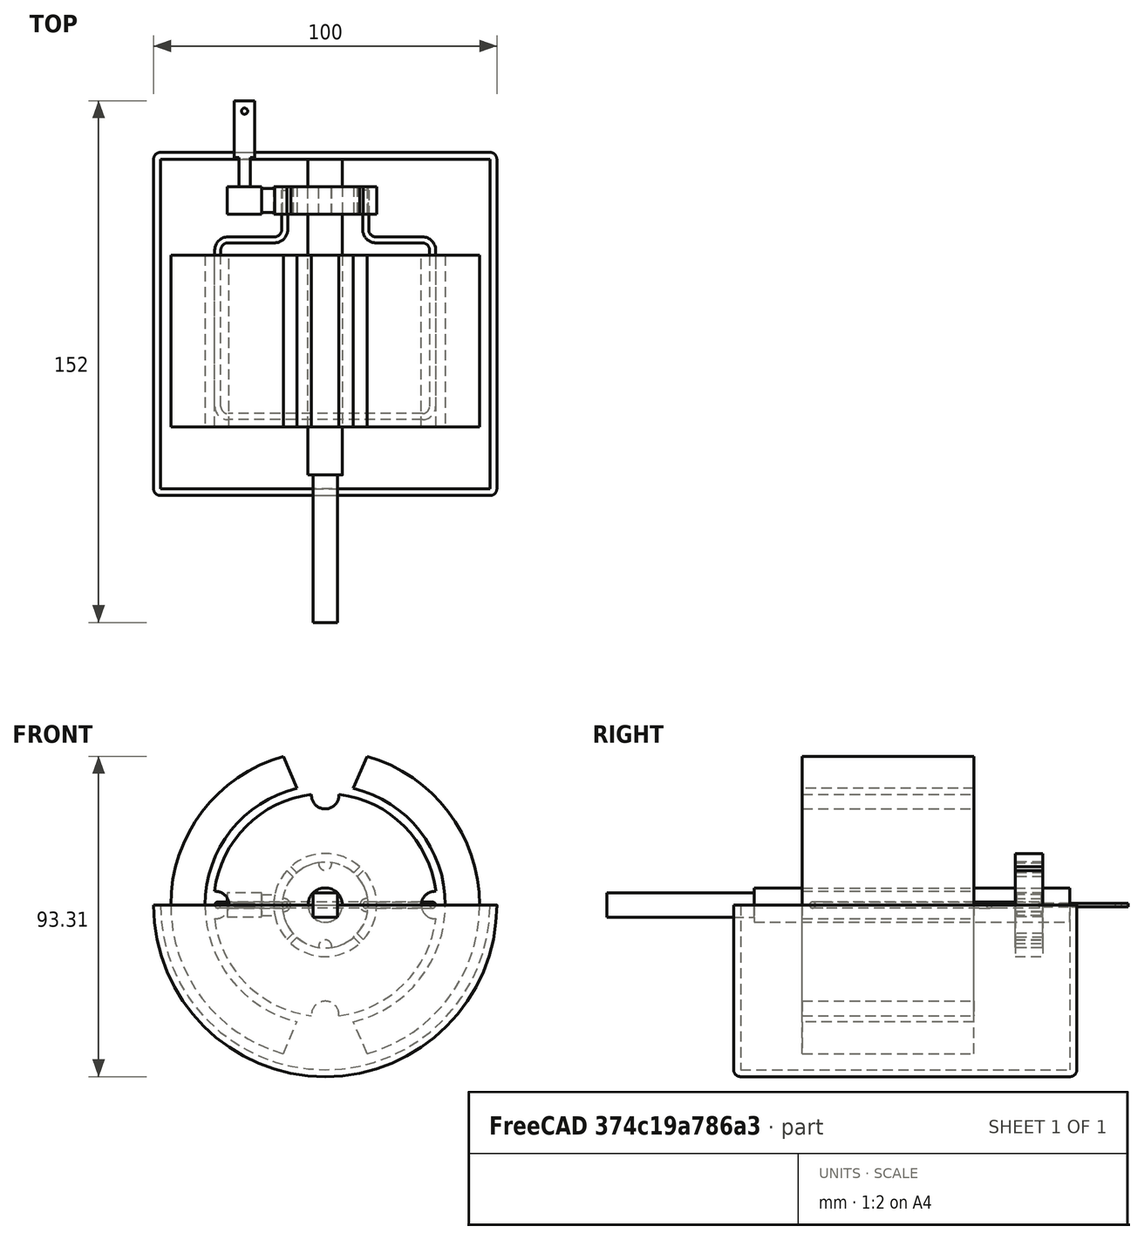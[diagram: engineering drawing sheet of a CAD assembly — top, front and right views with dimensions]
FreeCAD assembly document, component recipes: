
FREECAD ASSEMBLY — COMPONENT RECIPES ("DCmotor")

This assembly document has 15 components, labeled P0..P14 below (a component is one placed body or linked part). 15 of them carry a construction recipe — the FreeCAD feature program that regenerates the part from scratch, quoted from this document or its linked companion documents; the rest are supplied as boundary geometry only. No exploded tour is included for this assembly.
COMPONENT P0 — recipe-attached ("Brush001", modeled in this document).
Construction recipe (the document's own serialized feature program — sketch geometry with constraints, then the solid features built on it; lengths are millimeters unless a unit is written):

FEATURE [Sketcher::SketchObject] Sketch006
  ArcFitTolerance = 1e-06
  AttachmentSupport = -> [XZ_Plane002]
  FullyConstrained = true
  MakeInternals = false
  MapMode = 5
  Placement = pos=(0,0,0) rot=(1,0,0;1.5708rad)
  sketch-geometry (12):
    g0: LineSegment StartX=-18.57 StartY=3 StartZ=0 EndX=-18.57 EndY=-3 EndZ=0
    g1: LineSegment StartX=-18.57 StartY=-3 StartZ=0 EndX=-13.57 EndY=-3 EndZ=0
    g2: LineSegment StartX=-13.57 StartY=-3 StartZ=0 EndX=-13.57 EndY=3 EndZ=0
    g3: LineSegment StartX=-13.57 StartY=3 StartZ=0 EndX=-18.57 EndY=3 EndZ=0
    g4: LineSegment StartX=-28.57 StartY=3.5 StartZ=0 EndX=-28.57 EndY=-3.5 EndZ=0
    g5: LineSegment StartX=-28.57 StartY=-3.5 StartZ=0 EndX=-18.57 EndY=-3.5 EndZ=0
    g6: LineSegment StartX=-18.57 StartY=-3.5 StartZ=0 EndX=-18.57 EndY=3.5 EndZ=0
    g7: LineSegment StartX=-18.57 StartY=3.5 StartZ=0 EndX=-28.57 EndY=3.5 EndZ=0
    g8: LineSegment StartX=-31.07 StartY=0.75 StartZ=0 EndX=-31.07 EndY=-0.75 EndZ=0
    g9: LineSegment StartX=-31.07 StartY=-0.75 StartZ=0 EndX=-28.57 EndY=-0.75 EndZ=0
    g10: LineSegment StartX=-28.57 StartY=-0.75 StartZ=0 EndX=-28.57 EndY=0.75 EndZ=0
    g11: LineSegment StartX=-28.57 StartY=0.75 StartZ=0 EndX=-31.07 EndY=0.75 EndZ=0
  constraints (33):
    c: Coincident(g0,g1)
    c: Coincident(g1,g2)
    c: Coincident(g2,g3)
    c: Coincident(g3,g0)
    c: Vertical(g0)
    c: Horizontal(g1)
    c: Horizontal(g3)
    c: Symmetric(g1,g2,g-1)
    c: DistanceY(g-1,g2) = 3
    c: DistanceX(g0,g2) = 5
    c: DistanceX(g1,g-1) = 13.57
    c: Coincident(g4,g5)
    c: Coincident(g5,g6)
    c: Coincident(g6,g7)
    c: Coincident(g7,g4)
    c: Vertical(g4)
    c: Horizontal(g5)
    c: Horizontal(g7)
    c: Vertical(g6,g0)
    c: DistanceX(g4,g6) = 10
    c: DistanceY(g4,g4) = 7
    c: Symmetric(g5,g6,g-1)
    c: Coincident(g8,g9)
    c: Coincident(g9,g10)
    c: Coincident(g10,g11)
    c: Coincident(g11,g8)
    c: Vertical(g8)
    c: Horizontal(g9)
    c: Horizontal(g11)
    c: Vertical(g9,g4)
    c: Symmetric(g9,g10,g-1)
    c: DistanceY(g8,g8) = 1.5
    c: DistanceX(g8,g9) = 2.5
FEATURE [PartDesign::Pad] Pad002
  Direction = (0,-1,2e-16)
  Length = 8
  Length2 = 10
  Placement = pos=(0,0,0) rot=(1,0,0;1.5708rad)
  Profile = -> Sketch006
  ReferenceAxis = -> Sketch006 [N_Axis]
  Refine = true
  Suppressed = false
  Type = 0
FEATURE [Sketcher::SketchObject] Sketch007
  ArcFitTolerance = 1e-06
  AttachmentSupport = -> [Pad002]
  FullyConstrained = true
  MakeInternals = false
  MapMode = 5
  Placement = pos=(0,-8,4.2e-15) rot=(1,0,0;1.5708rad)
  sketch-geometry (1):
    g0: Circle CenterX=0 CenterY=0 CenterZ=0 NormalX=0 NormalY=0 NormalZ=1 AngleXU=0 Radius=15
  constraints (2):
    c: Diameter(g0) = 30
    c: Coincident(g0,g-1)
FEATURE [PartDesign::Pocket] Pocket004
  BaseFeature = -> Pad002
  Direction = (0,1,-2e-16)
  Length = 5
  Length2 = 5
  Placement = pos=(0,0,0) rot=(1,0,0;1.5708rad)
  Profile = -> Sketch007
  ReferenceAxis = -> Sketch007 [N_Axis]
  Refine = true
  Suppressed = false
  Type = 1
FEATURE [Sketcher::SketchObject] Sketch008
  ArcFitTolerance = 1e-06
  AttachmentSupport = -> [Pocket004]
  ExternalGeometry = -> [Pocket004]
  FullyConstrained = true
  MakeInternals = false
  MapMode = 5
  Placement = pos=(0,3e-16,0.75) rot=(0,0,1;3.14159rad)
  sketch-geometry (8):
    g0: LineSegment StartX=31.07 StartY=8 StartZ=0 EndX=28.57 EndY=8 EndZ=0
    g1: LineSegment StartX=28.57 StartY=8 StartZ=0 EndX=28.57 EndY=3.51 EndZ=0
    g2: LineSegment StartX=28.57 StartY=3.51 StartZ=0 EndX=31.07 EndY=3.51 EndZ=0
    g3: LineSegment StartX=31.07 StartY=3.51 StartZ=0 EndX=31.07 EndY=8 EndZ=0
    g4: LineSegment StartX=28.57 StartY=4.49 StartZ=0 EndX=28.57 EndY=0 EndZ=0
    g5: LineSegment StartX=28.57 StartY=0 StartZ=0 EndX=31.07 EndY=0 EndZ=0
    g6: LineSegment StartX=31.07 StartY=0 StartZ=0 EndX=31.07 EndY=4.49 EndZ=0
    g7: LineSegment StartX=31.07 StartY=4.49 StartZ=0 EndX=28.57 EndY=4.49 EndZ=0
  constraints (23):
    c: Coincident(g0,g1)
    c: Coincident(g1,g2)
    c: Coincident(g2,g3)
    c: Coincident(g3,g0)
    c: Horizontal(g0)
    c: Horizontal(g2)
    c: Vertical(g1)
    c: Vertical(g3)
    c: Coincident(g0,g-4)
    c: PointOnObject(g1,g-3)
    c: Coincident(g4,g5)
    c: Coincident(g5,g6)
    c: Coincident(g6,g7)
    c: Coincident(g7,g4)
    c: Vertical(g4)
    c: Vertical(g6)
    c: Horizontal(g5)
    c: Horizontal(g7)
    c: PointOnObject(g4,g-3)
    c: PointOnObject(g5,g-1)
    c: Vertical(g6,g2)
    c: Equal(g6,g3)
    c: DistanceY(g-1,g2) = 3.51
FEATURE [PartDesign::Pocket] Pocket005
  BaseFeature = -> Pocket004
  Direction = (0,0,-1)
  Length = 5
  Length2 = 5
  Placement = pos=(0,0,0) rot=(1,0,0;1.5708rad)
  Profile = -> Sketch008
  ReferenceAxis = -> Sketch008 [N_Axis]
  Refine = true
  Suppressed = false
  Type = 1
FEATURE [Sketcher::SketchObject] Sketch009
  ArcFitTolerance = 1e-06
  AttachmentSupport = -> [Pocket005]
  ExternalGeometry = -> [Pocket005]
  FullyConstrained = true
  MakeInternals = false
  MapMode = 5
  Placement = pos=(0,1.3e-15,3) rot=(0,0,1;3.14159rad)
  sketch-geometry (8):
    g0: LineSegment StartX=14.6969 StartY=8 StartZ=0 EndX=14.6969 EndY=7.5 EndZ=0
    g1: LineSegment StartX=14.6969 StartY=7.5 StartZ=0 EndX=18.57 EndY=7.5 EndZ=0
    g2: LineSegment StartX=18.57 StartY=7.5 StartZ=0 EndX=18.57 EndY=8 EndZ=0
    g3: LineSegment StartX=18.57 StartY=8 StartZ=0 EndX=14.6969 EndY=8 EndZ=0
    g4: LineSegment StartX=14.6969 StartY=0.5 StartZ=0 EndX=14.6969 EndY=-1e-16 EndZ=0
    g5: LineSegment StartX=14.6969 StartY=-1e-16 StartZ=0 EndX=18.57 EndY=-1e-16 EndZ=0
    g6: LineSegment StartX=18.57 StartY=-1e-16 StartZ=0 EndX=18.57 EndY=0.5 EndZ=0
    g7: LineSegment StartX=18.57 StartY=0.5 StartZ=0 EndX=14.6969 EndY=0.5 EndZ=0
  constraints (22):
    c: Coincident(g0,g1)
    c: Coincident(g1,g2)
    c: Coincident(g2,g3)
    c: Coincident(g3,g0)
    c: Vertical(g0)
    c: Vertical(g2)
    c: Horizontal(g1)
    c: Horizontal(g3)
    c: Coincident(g0,g-5)
    c: PointOnObject(g1,g-4)
    c: DistanceY(g1,g2) = 0.5
    c: Coincident(g4,g5)
    c: Coincident(g5,g6)
    c: Coincident(g6,g7)
    c: Coincident(g7,g4)
    c: Vertical(g4)
    c: Vertical(g6)
    c: Horizontal(g5)
    c: Horizontal(g7)
    c: PointOnObject(g4,g-5)
    c: Coincident(g5,g-4)
    c: DistanceY(g4,g4) = 0.5
FEATURE [PartDesign::Pocket] Pocket006
  BaseFeature = -> Pocket005
  Direction = (0,0,-1)
  Length = 5
  Length2 = 5
  Placement = pos=(0,0,0) rot=(1,0,0;1.5708rad)
  Profile = -> Sketch009
  ReferenceAxis = -> Sketch009 [N_Axis]
  Refine = true
  Suppressed = false
  Type = 1
FEATURE [PartDesign::Body] Body002  label="Brush"
  AllowCompound = false
  Group = -> [Sketch006,Pad002,Sketch007,Pocket004,Sketch008,Pocket005,Sketch009,Pocket006]
  Origin = -> Origin002
  Placement = pos=(0,15,0) rot=(0,0,1;0rad)
  Tip = -> Pocket006
COMPONENT P1 — same part as P0; its construction recipe is shown at P0.
COMPONENT P2 — recipe-attached ("BrushArms001", modeled in this document).
Construction recipe (the document's own serialized feature program — sketch geometry with constraints, then the solid features built on it; lengths are millimeters unless a unit is written):

FEATURE [Sketcher::SketchObject] Sketch016
  ArcFitTolerance = 1e-06
  AttachmentSupport = -> [XY_Plane007]
  FullyConstrained = true
  MakeInternals = false
  MapMode = 5
  sketch-geometry (9):
    g0: LineSegment StartX=-25.16 StartY=15 StartZ=0 EndX=-25.16 EndY=23.5 EndZ=0
    g1: LineSegment StartX=-25.16 StartY=23.5 StartZ=0 EndX=-26.49 EndY=23.5 EndZ=0
    g2: LineSegment StartX=-26.49 StartY=23.5 StartZ=0 EndX=-26.49 EndY=40 EndZ=0
    g3: LineSegment StartX=-26.49 StartY=40 StartZ=0 EndX=-20.5 EndY=40 EndZ=0
    g4: LineSegment StartX=-20.5 StartY=40 StartZ=0 EndX=-20.5 EndY=23.5 EndZ=0
    g5: LineSegment StartX=-20.5 StartY=23.5 StartZ=0 EndX=-21.83 EndY=23.5 EndZ=0
    g6: LineSegment StartX=-21.83 StartY=23.5 StartZ=0 EndX=-21.83 EndY=15 EndZ=0
    g7: LineSegment StartX=-21.83 StartY=15 StartZ=0 EndX=-25.16 EndY=15 EndZ=0
    g8: Circle CenterX=-23.5 CenterY=37 CenterZ=0 NormalX=0 NormalY=0 NormalZ=1 AngleXU=0 Radius=0.9
  constraints (27):
    c: Vertical(g0)
    c: Coincident(g0,g1)
    c: Coincident(g1,g2)
    c: Vertical(g2)
    c: Coincident(g2,g3)
    c: Horizontal(g3)
    c: Coincident(g3,g4)
    c: Vertical(g4)
    c: Coincident(g4,g5)
    c: Horizontal(g5)
    c: Coincident(g5,g6)
    c: Vertical(g6)
    c: Coincident(g6,g7)
    c: Coincident(g7,g0)
    c: Horizontal(g7)
    c: DistanceY(g-1,g0) = 15
    c: Horizontal(g1,g0)
    c: Horizontal(g5,g0)
    c: DistanceX(g6,g-1) = 21.83
    c: DistanceX(g0,g-1) = 25.16
    c: DistanceX(g4,g-1) = 20.5
    c: Equal(g5,g1)
    c: DistanceY(g-1,g4) = 23.5
    c: DistanceY(g-1,g2) = 40
    c: DistanceX(g8,g-1) = 23.5
    c: Diameter(g8) = 1.8
    c: DistanceY(g-1,g8) = 37
FEATURE [PartDesign::Pad] Pad005
  Direction = (0,0,1)
  Length = 1
  Length2 = 10
  Profile = -> Sketch016
  ReferenceAxis = -> Sketch016 [N_Axis]
  Refine = true
  Suppressed = false
  Type = 0
FEATURE [PartDesign::Body] Body006  label="BrushArms"
  AllowCompound = false
  Group = -> [Sketch016,Pad005]
  Origin = -> Origin007
  Placement = pos=(0,0,-0.5) rot=(0,0,1;0rad)
  Tip = -> Pad005
COMPONENT P3 — same part as P2; its construction recipe is shown at P2.
COMPONENT P4 — recipe-attached ("Case001", modeled in this document).
Construction recipe (the document's own serialized feature program — sketch geometry with constraints, then the solid features built on it; lengths are millimeters unless a unit is written):

FEATURE [Sketcher::SketchObject] Sketch021
  ArcFitTolerance = 1e-06
  AttachmentSupport = -> [XZ_Plane010]
  FullyConstrained = true
  MakeInternals = false
  MapMode = 5
  Placement = pos=(0,0,0) rot=(1,0,0;1.5708rad)
  sketch-geometry (2):
    g0: ArcOfCircle CenterX=0 CenterY=0 CenterZ=0 NormalX=0 NormalY=0 NormalZ=1 AngleXU=0 Radius=50 StartAngle=3.14159 EndAngle=6.28319
    g1: LineSegment StartX=50 StartY=-1.22e-14 StartZ=0 EndX=-50 EndY=1.73205e-05 EndZ=0
  constraints (6):
    c: Angle(g0) = 3.14159
    c: Coincident(g0,g-1)
    c: PointOnObject(g0,g-1)
    c: DistanceX(g-1,g0) = 50
    c: Coincident(g1,g0)
    c: Coincident(g1,g0)
FEATURE [PartDesign::Pad] Pad008
  Direction = (0,-1,2e-16)
  Length = 100
  Length2 = 10
  Placement = pos=(0,0,0) rot=(1,0,0;1.5708rad)
  Profile = -> Sketch021
  ReferenceAxis = -> Sketch021 [N_Axis]
  Refine = true
  Suppressed = false
  Type = 0
FEATURE [Sketcher::SketchObject] Sketch022
  ArcFitTolerance = 1e-06
  AttachmentSupport = -> [XZ_Plane010]
  FullyConstrained = true
  MakeInternals = false
  MapMode = 5
  Placement = pos=(0,0,0) rot=(1,0,0;1.5708rad)
  sketch-geometry (2):
    g0: ArcOfCircle CenterX=0 CenterY=0 CenterZ=0 NormalX=0 NormalY=0 NormalZ=1 AngleXU=0 Radius=48 StartAngle=3.14159 EndAngle=6.28319
    g1: LineSegment StartX=48 StartY=0 StartZ=0 EndX=-48 EndY=5.9e-15 EndZ=0
  constraints (6):
    c: Radius(g0) = 48
    c: Coincident(g0,g-1)
    c: PointOnObject(g0,g-1)
    c: PointOnObject(g0,g-1)
    c: Coincident(g1,g0)
    c: Coincident(g1,g0)
FEATURE [PartDesign::Pocket] Pocket011
  BaseFeature = -> Pad008
  Direction = (0,1,-2e-16)
  Length = 5
  Length2 = 5
  Placement = pos=(0,0,0) rot=(1,0,0;1.5708rad)
  Profile = -> Sketch022
  ReferenceAxis = -> Sketch022 [N_Axis]
  Refine = true
  Reversed = true
  Suppressed = false
  Type = 1
FEATURE [Sketcher::SketchObject] Sketch023
  ArcFitTolerance = 1e-06
  AttachmentSupport = -> [XZ_Plane010]
  FullyConstrained = true
  MakeInternals = false
  MapMode = 5
  Placement = pos=(0,0,0) rot=(1,0,0;1.5708rad)
  sketch-geometry (2):
    g0: ArcOfCircle CenterX=0 CenterY=0 CenterZ=0 NormalX=0 NormalY=0 NormalZ=1 AngleXU=0 Radius=48.02 StartAngle=3.14159 EndAngle=6.28319
    g1: LineSegment StartX=-48.02 StartY=0 StartZ=0 EndX=48.02 EndY=0 EndZ=0
  constraints (6):
    c: Radius(g0) = 48.02
    c: Coincident(g0,g-1)
    c: PointOnObject(g0,g-1)
    c: PointOnObject(g0,g-1)
    c: Coincident(g1,g0)
    c: Coincident(g1,g0)
FEATURE [PartDesign::Pad] Pad009
  BaseFeature = -> Pocket011
  Direction = (0,-1,2e-16)
  Length = 2
  Length2 = 10
  Placement = pos=(0,0,0) rot=(1,0,0;1.5708rad)
  Profile = -> Sketch023
  ReferenceAxis = -> Sketch023 [N_Axis]
  Refine = true
  Suppressed = false
  Type = 0
FEATURE [Sketcher::SketchObject] Sketch024
  ArcFitTolerance = 1e-06
  AttachmentSupport = -> [Pad009]
  FullyConstrained = true
  MakeInternals = false
  MapMode = 5
  Placement = pos=(0,-100,2.2e-14) rot=(1,0,0;1.5708rad)
  sketch-geometry (2):
    g0: ArcOfCircle CenterX=0 CenterY=0 CenterZ=0 NormalX=0 NormalY=0 NormalZ=1 AngleXU=0 Radius=48.02 StartAngle=3.14159 EndAngle=6.28319
    g1: LineSegment StartX=-48.02 StartY=5.9e-15 StartZ=0 EndX=48.02 EndY=0 EndZ=0
  constraints (6):
    c: Radius(g0) = 48.02
    c: Coincident(g0,g-1)
    c: PointOnObject(g0,g-1)
    c: PointOnObject(g0,g-1)
    c: Coincident(g1,g0)
    c: Coincident(g1,g0)
FEATURE [PartDesign::Pad] Pad010
  BaseFeature = -> Pad009
  Direction = (0,-1,2e-16)
  Length = 2
  Length2 = 10
  Placement = pos=(0,0,0) rot=(1,0,0;1.5708rad)
  Profile = -> Sketch024
  ReferenceAxis = -> Sketch024 [N_Axis]
  Refine = true
  Reversed = true
  Suppressed = false
  Type = 0
FEATURE [PartDesign::Fillet] Fillet
  Base = -> Pad010 [Edge8]
  BaseFeature = -> Pad010
  Placement = pos=(0,0,0) rot=(1,0,0;1.5708rad)
  Radius = 2
  Refine = true
  SupportTransform = false
  Suppressed = false
  UseAllEdges = false
FEATURE [PartDesign::Fillet] Fillet001
  Base = -> Fillet [Edge3]
  BaseFeature = -> Fillet
  Placement = pos=(0,0,0) rot=(1,0,0;1.5708rad)
  Radius = 2
  Refine = true
  SupportTransform = false
  Suppressed = false
  UseAllEdges = false
FEATURE [Sketcher::SketchObject] Sketch025
  ArcFitTolerance = 1e-06
  AttachmentSupport = -> [XZ_Plane010]
  FullyConstrained = true
  MakeInternals = false
  MapMode = 5
  Placement = pos=(0,0,0) rot=(1,0,0;1.5708rad)
FEATURE [PartDesign::Body] Body009  label="Case"
  AllowCompound = false
  Group = -> [Sketch021,Pad008,Sketch022,Pocket011,Sketch023,Pad009,Sketch024,Pad010,Fillet,Fillet001,Sketch025]
  Origin = -> Origin010
  Placement = pos=(0,25,0) rot=(0,0,1;0rad)
  Tip = -> Fillet001
COMPONENT P5 — same part as P4; its construction recipe is shown at P4.
COMPONENT P6 — recipe-attached ("Commutator001", modeled in this document).
Construction recipe (the document's own serialized feature program — sketch geometry with constraints, then the solid features built on it; lengths are millimeters unless a unit is written):

FEATURE [Sketcher::SketchObject] Sketch
  ArcFitTolerance = 1e-06
  AttachmentSupport = -> [XZ_Plane]
  FullyConstrained = true
  MakeInternals = false
  MapMode = 5
  Placement = pos=(0,0,0) rot=(1,0,0;1.5708rad)
  sketch-geometry (1):
    g0: Circle CenterX=0 CenterY=0 CenterZ=0 NormalX=0 NormalY=0 NormalZ=1 AngleXU=0 Radius=15
  constraints (2):
    c: Coincident(g0,g-1)
    c: Diameter(g0) = 30
FEATURE [PartDesign::Pad] Pad
  Direction = (0,-1,2e-16)
  Length = 8
  Length2 = 10
  Placement = pos=(0,0,0) rot=(1,0,0;1.5708rad)
  Profile = -> Sketch
  ReferenceAxis = -> Sketch [N_Axis]
  Refine = true
  Suppressed = false
  Type = 0
FEATURE [Sketcher::SketchObject] Sketch001
  ArcFitTolerance = 1e-06
  AttachmentSupport = -> [Pad]
  FullyConstrained = true
  MakeInternals = false
  MapMode = 5
  Placement = pos=(0,-8,0) rot=(1,0,0;1.5708rad)
  sketch-geometry (1):
    g0: Circle CenterX=0 CenterY=0 CenterZ=0 NormalX=0 NormalY=0 NormalZ=1 AngleXU=0 Radius=12.5
  constraints (2):
    c: Diameter(g0) = 25
    c: Coincident(g0,g-1)
FEATURE [PartDesign::Pocket] Pocket
  BaseFeature = -> Pad
  Direction = (0,1,-2e-16)
  Length = 5
  Length2 = 5
  Placement = pos=(0,0,0) rot=(1,0,0;1.5708rad)
  Profile = -> Sketch001
  ReferenceAxis = -> Sketch001 [N_Axis]
  Refine = true
  Suppressed = false
  Type = 1
FEATURE [Sketcher::SketchObject] Sketch002
  ArcFitTolerance = 1e-06
  AttachmentSupport = -> [Pocket]
  ExternalGeometry = -> [Pocket]
  FullyConstrained = true
  MakeInternals = false
  MapMode = 5
  Placement = pos=(0,-8,0) rot=(1,0,0;1.5708rad)
  sketch-geometry (8):
    g0: LineSegment StartX=-0.75 StartY=18.87 StartZ=0 EndX=-0.75 EndY=-18.87 EndZ=0
    g1: LineSegment StartX=-0.75 StartY=-18.87 StartZ=0 EndX=0.75 EndY=-18.87 EndZ=0
    g2: LineSegment StartX=0.75 StartY=-18.87 StartZ=0 EndX=0.75 EndY=18.87 EndZ=0
    g3: LineSegment StartX=0.75 StartY=18.87 StartZ=0 EndX=-0.75 EndY=18.87 EndZ=0
    g4: LineSegment StartX=-17.13 StartY=0.75 StartZ=0 EndX=-17.13 EndY=-0.75 EndZ=0
    g5: LineSegment StartX=-17.13 StartY=-0.75 StartZ=0 EndX=17.73 EndY=-0.75 EndZ=0
    g6: LineSegment StartX=17.73 StartY=-0.75 StartZ=0 EndX=17.73 EndY=0.75 EndZ=0
    g7: LineSegment StartX=17.73 StartY=0.75 StartZ=0 EndX=-17.13 EndY=0.75 EndZ=0
  constraints (21):
    c: Coincident(g0,g1)
    c: Coincident(g1,g2)
    c: Coincident(g2,g3)
    c: Coincident(g3,g0)
    c: Vertical(g0)
    c: Horizontal(g1)
    c: Symmetric(g0,g2,g-2)
    c: DistanceX(g0,g-1) = 0.75
    c: Coincident(g4,g5)
    c: Coincident(g5,g6)
    c: Coincident(g6,g7)
    c: Coincident(g7,g4)
    c: Vertical(g4)
    c: Horizontal(g5)
    c: Horizontal(g7)
    c: Symmetric(g5,g6,g-1)
    c: DistanceY(g5,g-1) = 0.75
    c: Symmetric(g1,g2,g-1)
    c: DistanceY(g1,g-1) = 18.87
    c: DistanceX(g4,g-1) = 17.13
    c: DistanceX(g-1,g5) = 17.73
FEATURE [PartDesign::Pocket] Pocket001
  BaseFeature = -> Pocket
  Direction = (0,1,-2e-16)
  Length = 5
  Length2 = 5
  Placement = pos=(0,0,0) rot=(1,0,0;1.5708rad)
  Profile = -> Sketch002
  ReferenceAxis = -> Sketch002 [N_Axis]
  Refine = true
  Suppressed = false
  Type = 1
FEATURE [PartDesign::Body] Body  label="Commutator"
  AllowCompound = true
  Group = -> [Sketch,Pad,Sketch001,Pocket,Sketch002,Pocket001]
  Origin = -> Origin
  Placement = pos=(0,15,1.08e-14) rot=(0,1,0;0.785398rad)
  Tip = -> Pocket001
COMPONENT P7 — recipe-attached ("CommutatorSupport001", modeled in this document).
Construction recipe (the document's own serialized feature program — sketch geometry with constraints, then the solid features built on it; lengths are millimeters unless a unit is written):

FEATURE [Sketcher::SketchObject] Sketch017
  ArcFitTolerance = 1e-06
  AttachmentSupport = -> [XZ_Plane008]
  FullyConstrained = true
  MakeInternals = false
  MapMode = 5
  Placement = pos=(0,0,0) rot=(1,0,0;1.5708rad)
  sketch-geometry (1):
    g0: Circle CenterX=0 CenterY=0 CenterZ=0 NormalX=0 NormalY=0 NormalZ=1 AngleXU=0 Radius=12.5
  constraints (2):
    c: Diameter(g0) = 25
    c: Coincident(g0,g-1)
FEATURE [PartDesign::Pad] Pad006
  Direction = (0,-1,2e-16)
  Length = 8
  Length2 = 10
  Placement = pos=(0,0,0) rot=(1,0,0;1.5708rad)
  Profile = -> Sketch017
  ReferenceAxis = -> Sketch017 [N_Axis]
  Refine = true
  Suppressed = false
  Type = 0
FEATURE [Sketcher::SketchObject] Sketch018
  ArcFitTolerance = 1e-06
  AttachmentSupport = -> [XZ_Plane008]
  FullyConstrained = true
  MakeInternals = false
  MapMode = 5
  Placement = pos=(0,0,0) rot=(1,0,0;1.5708rad)
  sketch-geometry (4):
    g0: Circle CenterX=12 CenterY=0 CenterZ=0 NormalX=0 NormalY=0 NormalZ=1 AngleXU=0 Radius=1.875
    g1: Circle CenterX=-12 CenterY=0 CenterZ=0 NormalX=0 NormalY=0 NormalZ=1 AngleXU=0 Radius=1.875
    g2: Circle CenterX=0 CenterY=12 CenterZ=0 NormalX=0 NormalY=0 NormalZ=1 AngleXU=0 Radius=1.875
    g3: Circle CenterX=0 CenterY=-12 CenterZ=0 NormalX=0 NormalY=0 NormalZ=1 AngleXU=0 Radius=1.875
  constraints (10):
    c: Diameter(g0) = 3.75
    c: PointOnObject(g0,g-1)
    c: DistanceX(g-1,g0) = 12
    c: Symmetric(g1,g0,g-2)
    c: Equal(g1,g0)
    c: PointOnObject(g2,g-2)
    c: Equal(g2,g1)
    c: DistanceY(g-1,g2) = 12
    c: Equal(g3,g1)
    c: Symmetric(g3,g2,g-1)
FEATURE [PartDesign::Pocket] Pocket009
  BaseFeature = -> Pad006
  Direction = (0,1,-2e-16)
  Length = 5
  Length2 = 5
  Placement = pos=(0,0,0) rot=(1,0,0;1.5708rad)
  Profile = -> Sketch018
  ReferenceAxis = -> Sketch018 [N_Axis]
  Refine = true
  Reversed = true
  Suppressed = false
  Type = 1
FEATURE [PartDesign::Body] Body007  label="CommutatorSupport"
  AllowCompound = false
  Group = -> [Sketch017,Pad006,Sketch018,Pocket009]
  Origin = -> Origin008
  Placement = pos=(0,15,0) rot=(0,1,0;0rad)
  Tip = -> Pocket009
COMPONENT P8 — recipe-attached ("NorthMagnet001", modeled in this document).
Construction recipe (the document's own serialized feature program — sketch geometry with constraints, then the solid features built on it; lengths are millimeters unless a unit is written):

FEATURE [Sketcher::SketchObject] Sketch003
  ArcFitTolerance = 1e-06
  AttachmentSupport = -> [XZ_Plane001]
  FullyConstrained = true
  MakeInternals = false
  MapMode = 5
  Placement = pos=(0,0,0) rot=(1,0,0;1.5708rad)
  sketch-geometry (1):
    g0: Circle CenterX=0 CenterY=0 CenterZ=0 NormalX=0 NormalY=0 NormalZ=1 AngleXU=0 Radius=45
  constraints (2):
    c: Coincident(g0,g-1)
    c: Diameter(g0) = 90
FEATURE [PartDesign::Pad] Pad001
  Direction = (0,-1,2e-16)
  Length = 50
  Length2 = 10
  Placement = pos=(0,0,0) rot=(1,0,0;1.5708rad)
  Profile = -> Sketch003
  ReferenceAxis = -> Sketch003 [N_Axis]
  Refine = true
  Suppressed = false
  Type = 0
FEATURE [Sketcher::SketchObject] Sketch004
  ArcFitTolerance = 1e-06
  AttachmentSupport = -> [Pad001]
  FullyConstrained = true
  MakeInternals = false
  MapMode = 5
  Placement = pos=(0,-50,0) rot=(1,0,0;1.5708rad)
  sketch-geometry (1):
    g0: Circle CenterX=0 CenterY=0 CenterZ=0 NormalX=0 NormalY=0 NormalZ=1 AngleXU=0 Radius=35
  constraints (2):
    c: Diameter(g0) = 70
    c: Coincident(g0,g-1)
FEATURE [PartDesign::Pocket] Pocket002
  BaseFeature = -> Pad001
  Direction = (0,1,-2e-16)
  Length = 5
  Length2 = 5
  Placement = pos=(0,0,0) rot=(1,0,0;1.5708rad)
  Profile = -> Sketch004
  ReferenceAxis = -> Sketch004 [N_Axis]
  Refine = true
  Suppressed = false
  Type = 1
FEATURE [Sketcher::SketchObject] Sketch005
  ArcFitTolerance = 1e-06
  AttachmentSupport = -> [Pocket002]
  ExternalGeometry = -> [Pocket002]
  FullyConstrained = true
  MakeInternals = false
  MapMode = 5
  Placement = pos=(0,-50,0) rot=(1,0,0;1.5708rad)
  sketch-geometry (8):
    g0: LineSegment StartX=-13 StartY=45.18 StartZ=0 EndX=13 EndY=45.18 EndZ=0
    g1: LineSegment StartX=-8.2 StartY=34 StartZ=0 EndX=8.2 EndY=34 EndZ=0
    g2: LineSegment StartX=-13 StartY=45.18 StartZ=0 EndX=-8.2 EndY=34 EndZ=0
    g3: LineSegment StartX=8.2 StartY=34 StartZ=0 EndX=13 EndY=45.18 EndZ=0
    g4: LineSegment StartX=-8.2 StartY=-34 StartZ=0 EndX=8.2 EndY=-34 EndZ=0
    g5: LineSegment StartX=8.2 StartY=-34 StartZ=0 EndX=13 EndY=-45.18 EndZ=0
    g6: LineSegment StartX=13 StartY=-45.18 StartZ=0 EndX=-13 EndY=-45.18 EndZ=0
    g7: LineSegment StartX=-13 StartY=-45.18 StartZ=0 EndX=-8.2 EndY=-34 EndZ=0
  constraints (20):
    c: DistanceX(g0,g-1) = 13
    c: Symmetric(g0,g0,g-2)
    c: Symmetric(g1,g1,g-2)
    c: DistanceX(g1,g-1) = 8.2
    c: Coincident(g2,g0)
    c: Coincident(g2,g1)
    c: Coincident(g3,g1)
    c: Coincident(g3,g0)
    c: DistanceY(g-1,g1) = 34
    c: DistanceY(g-1,g0) = 45.18
    c: Coincident(g4,g5)
    c: Coincident(g5,g6)
    c: Coincident(g6,g7)
    c: Coincident(g7,g4)
    c: Vertical(g4,g1)
    c: Symmetric(g4,g4,g-2)
    c: Symmetric(g6,g5,g-2)
    c: Vertical(g6,g0)
    c: Equal(g2,g7)
    c: DistanceY(g4,g-1) = 34
FEATURE [PartDesign::Pocket] Pocket003
  BaseFeature = -> Pocket002
  Direction = (0,1,-2e-16)
  Length = 5
  Length2 = 5
  Placement = pos=(0,0,0) rot=(1,0,0;1.5708rad)
  Profile = -> Sketch005
  ReferenceAxis = -> Sketch005 [N_Axis]
  Refine = true
  Suppressed = false
  Type = 1
FEATURE [PartDesign::Body] Body001  label="NorthMagnet"
  AllowCompound = false
  Group = -> [Sketch003,Pad001,Sketch004,Pocket002,Sketch005,Pocket003]
  Origin = -> Origin001
  Placement = pos=(0,-5,0) rot=(0,0,1;0rad)
  Tip = -> Pocket003
COMPONENT P9 — recipe-attached ("Rotor001", modeled in this document).
Construction recipe (the document's own serialized feature program — sketch geometry with constraints, then the solid features built on it; lengths are millimeters unless a unit is written):

FEATURE [Sketcher::SketchObject] Sketch013
  ArcFitTolerance = 1e-06
  AttachmentSupport = -> [XY_Plane004]
  FullyConstrained = true
  MakeInternals = false
  MapMode = 5
  sketch-geometry (19):
    g0: LineSegment StartX=11.8 StartY=11 StartZ=0 EndX=11.8 EndY=-0.5 EndZ=0
    g1: LineSegment StartX=14.8 StartY=-3.5 StartZ=0 EndX=28.3 EndY=-3.5 EndZ=0
    g2: LineSegment StartX=31.3 StartY=-6.5 StartZ=0 EndX=31.3 EndY=-52 EndZ=0
    g3: LineSegment StartX=28.3 StartY=-55 StartZ=0 EndX=-28.3 EndY=-55 EndZ=0
    g4: LineSegment StartX=-31.3 StartY=-52 StartZ=0 EndX=-31.3 EndY=-6.5 EndZ=0
    g5: LineSegment StartX=-28.3 StartY=-3.5 StartZ=0 EndX=-14.8 EndY=-3.5 EndZ=0
    g6: LineSegment StartX=-11.8 StartY=-0.5 StartZ=0 EndX=-11.8 EndY=11 EndZ=0
    g7: ArcOfCircle CenterX=28.3 CenterY=-6.5 CenterZ=0 NormalX=0 NormalY=0 NormalZ=1 AngleXU=0 Radius=3 StartAngle=0 EndAngle=1.5708
    g8: GeomPoint [constr] X=31.3 Y=-3.5 Z=0
    g9: ArcOfCircle CenterX=28.3 CenterY=-52 CenterZ=0 NormalX=0 NormalY=0 NormalZ=1 AngleXU=0 Radius=3 StartAngle=4.71239 EndAngle=6.28319
    g10: GeomPoint [constr] X=31.3 Y=-55 Z=0
    g11: ArcOfCircle CenterX=-28.3 CenterY=-6.5 CenterZ=0 NormalX=0 NormalY=0 NormalZ=1 AngleXU=0 Radius=3 StartAngle=1.5708 EndAngle=3.14159
    g12: GeomPoint [constr] X=-31.3 Y=-3.5 Z=0
    g13: ArcOfCircle CenterX=-28.3 CenterY=-52 CenterZ=0 NormalX=0 NormalY=0 NormalZ=1 AngleXU=0 Radius=3 StartAngle=3.14159 EndAngle=4.71239
    g14: GeomPoint [constr] X=-31.3 Y=-55 Z=0
    g15: ArcOfCircle CenterX=14.8 CenterY=-0.5 CenterZ=0 NormalX=0 NormalY=0 NormalZ=1 AngleXU=0 Radius=3 StartAngle=3.14159 EndAngle=4.71239
    g16: GeomPoint [constr] X=11.8 Y=-3.5 Z=0
    g17: ArcOfCircle CenterX=-14.8 CenterY=-0.5 CenterZ=0 NormalX=0 NormalY=0 NormalZ=1 AngleXU=0 Radius=3 StartAngle=4.71239 EndAngle=6.28319
    g18: GeomPoint [constr] X=-11.8 Y=-3.5 Z=0
  constraints (44):
    c: Vertical(g0)
    c: Horizontal(g1)
    c: Vertical(g2)
    c: Vertical(g4)
    c: Horizontal(g5)
    c: Vertical(g6)
    c: Symmetric(g6,g0,g-2)
    c: Horizontal(g16,g18)
    c: Symmetric(g10,g14,g-2)
    c: DistanceX(g6,g-1) = 11.8
    c: DistanceY(g-1,g6) = 11
    c: DistanceX(g12,g18) = 19.5
    c: DistanceY(g12,g-1) = 3.5
    c: DistanceY(g14,g-1) = 55
    c: PointOnObject(g8,g1)
    c: PointOnObject(g8,g2)
    c: Tangent(g1,g7) = 1.5708
    c: Tangent(g2,g7) = 1.5708
    c: DistanceX(g7,g2) = 3
    c: PointOnObject(g10,g2)
    c: PointOnObject(g10,g3)
    c: Tangent(g2,g9) = 1.5708
    c: Tangent(g3,g9) = 1.5708
    c: PointOnObject(g12,g4)
    c: PointOnObject(g12,g5)
    c: Tangent(g4,g11) = 1.5708
    c: Tangent(g5,g11) = 1.5708
    c: PointOnObject(g14,g3)
    c: PointOnObject(g14,g4)
    c: Tangent(g3,g13) = 1.5708
    c: Tangent(g4,g13) = 1.5708
    c: Vertical(g1,g3)
    c: Horizontal(g2,g4)
    c: Vertical(g3,g5)
    c: PointOnObject(g16,g0)
    c: PointOnObject(g16,g1)
    c: Tangent(g0,g15) = -1.5708
    c: Tangent(g1,g15) = -1.5708
    c: PointOnObject(g18,g5)
    c: PointOnObject(g18,g6)
    c: Tangent(g5,g17) = -1.5708
    c: Tangent(g6,g17) = -1.5708
    c: Equal(g11,g17)
    c: Equal(g17,g15)
FEATURE [Sketcher::SketchObject] Sketch014
  ArcFitTolerance = 1e-06
  AttachmentSupport = -> [XZ_Plane004]
  FullyConstrained = true
  MakeInternals = false
  MapMode = 5
  Placement = pos=(0,0,0) rot=(1,0,0;1.5708rad)
  sketch-geometry (1):
    g0: Circle CenterX=11.8 CenterY=0 CenterZ=0 NormalX=0 NormalY=0 NormalZ=1 AngleXU=0 Radius=0.875
  constraints (3):
    c: Diameter(g0) = 1.75
    c: PointOnObject(g0,g-1)
    c: DistanceX(g-1,g0) = 11.8
FEATURE [PartDesign::AdditivePipe] AdditivePipe
  AuxilleryCurvelinear = true
  AuxillerySpineTangent = false
  Binormal = (0,0,0)
  Mode = 0
  Placement = pos=(0,0,0) rot=(1,0,0;1.5708rad)
  Profile = -> Sketch014
  Refine = true
  Spine = -> Sketch013
  SpineTangent = false
  Suppressed = false
  Transformation = 0
  Transition = 0
FEATURE [PartDesign::Body] Body004  label="Rotor"
  AllowCompound = false
  Group = -> [Sketch013,Sketch014,AdditivePipe]
  Origin = -> Origin004
  Placement = pos=(0,3,0) rot=(0,1,0;0rad)
  Tip = -> AdditivePipe
COMPONENT P10 — same part as P9; its construction recipe is shown at P9.
COMPONENT P11 — recipe-attached ("RotorSupport001", modeled in this document).
Construction recipe (the document's own serialized feature program — sketch geometry with constraints, then the solid features built on it; lengths are millimeters unless a unit is written):

FEATURE [Sketcher::SketchObject] Sketch019
  ArcFitTolerance = 1e-06
  AttachmentSupport = -> [XZ_Plane009]
  FullyConstrained = true
  MakeInternals = false
  MapMode = 5
  Placement = pos=(0,0,0) rot=(1,0,0;1.5708rad)
  sketch-geometry (1):
    g0: Circle CenterX=0 CenterY=0 CenterZ=0 NormalX=0 NormalY=0 NormalZ=1 AngleXU=0 Radius=32.5
  constraints (2):
    c: Diameter(g0) = 65
    c: Coincident(g0,g-1)
FEATURE [PartDesign::Pad] Pad007
  Direction = (0,-1,2e-16)
  Length = 50
  Length2 = 10
  Placement = pos=(0,0,0) rot=(1,0,0;1.5708rad)
  Profile = -> Sketch019
  ReferenceAxis = -> Sketch019 [N_Axis]
  Refine = true
  Suppressed = false
  Type = 0
FEATURE [Sketcher::SketchObject] Sketch020
  ArcFitTolerance = 1e-06
  AttachmentSupport = -> [Pad007]
  FullyConstrained = true
  MakeInternals = false
  MapMode = 5
  Placement = pos=(0,0,0) rot=(-1,0,0;1.5708rad)
  sketch-geometry (4):
    g0: Circle CenterX=32 CenterY=0 CenterZ=0 NormalX=0 NormalY=0 NormalZ=1 AngleXU=0 Radius=4
    g1: Circle CenterX=-32 CenterY=0 CenterZ=0 NormalX=0 NormalY=0 NormalZ=1 AngleXU=0 Radius=4
    g2: Circle CenterX=0 CenterY=-32 CenterZ=0 NormalX=0 NormalY=0 NormalZ=1 AngleXU=0 Radius=4
    g3: Circle CenterX=-2e-16 CenterY=32 CenterZ=0 NormalX=0 NormalY=0 NormalZ=1 AngleXU=0 Radius=4
  constraints (10):
    c: PointOnObject(g0,g-1)
    c: Diameter(g0) = 8
    c: DistanceX(g-1,g0) = 32
    c: Symmetric(g1,g0,g-2)
    c: Equal(g1,g0)
    c: PointOnObject(g2,g-2)
    c: DistanceY(g2,g-1) = 32
    c: Symmetric(g3,g2,g-1)
    c: Equal(g0,g2)
    c: Equal(g3,g0)
FEATURE [PartDesign::Pocket] Pocket010
  BaseFeature = -> Pad007
  Direction = (0,-1,-2e-16)
  Length = 5
  Length2 = 5
  Placement = pos=(0,0,0) rot=(1,0,0;1.5708rad)
  Profile = -> Sketch020
  ReferenceAxis = -> Sketch020 [N_Axis]
  Refine = true
  Suppressed = false
  Type = 1
FEATURE [PartDesign::Body] Body008  label="RotorSupport"
  AllowCompound = false
  Group = -> [Sketch019,Pad007,Sketch020,Pocket010]
  Origin = -> Origin009
  Placement = pos=(0,-5,0) rot=(0,1,0;0rad)
  Tip = -> Pocket010
COMPONENT P12 — recipe-attached ("anchor", modeled in this document).
Construction recipe (the document's own serialized feature program — sketch geometry with constraints, then the solid features built on it; lengths are millimeters unless a unit is written):

FEATURE [Sketcher::SketchObject] Sketch015
  ArcFitTolerance = 1e-06
  AttachmentSupport = -> [XZ_Plane006]
  FullyConstrained = true
  MakeInternals = false
  MapMode = 5
  Placement = pos=(0,0,0) rot=(1,0,0;1.5708rad)
  sketch-geometry (1):
    g0: Circle CenterX=0 CenterY=0 CenterZ=0 NormalX=0 NormalY=0 NormalZ=1 AngleXU=0 Radius=5
  constraints (2):
    c: Coincident(g0,g-1)
    c: Diameter(g0) = 10
FEATURE [PartDesign::Pad] Pad004
  Direction = (0,-1,2e-16)
  Length = 135
  Length2 = 10
  Placement = pos=(0,0,0) rot=(1,0,0;1.5708rad)
  Profile = -> Sketch015 [Edge1]
  ReferenceAxis = -> Sketch015 [N_Axis]
  Refine = true
  Suppressed = false
  Type = 0
FEATURE [Sketcher::SketchObject] Sketch026
  ArcFitTolerance = 1e-06
  AttachmentSupport = -> [Pad004]
  ExternalGeometry = -> [Pad004]
  FullyConstrained = true
  MakeInternals = false
  MapMode = 5
  Placement = pos=(0,-135,0) rot=(1,0,0;1.5708rad)
  sketch-geometry (6):
    g0: LineSegment StartX=3.53106 StartY=-3.54 StartZ=0 EndX=3.53106 EndY=3.54 EndZ=0
    g1: LineSegment StartX=3.53106 StartY=3.54 StartZ=0 EndX=-3.53106 EndY=3.54 EndZ=0
    g2: LineSegment StartX=-3.53106 StartY=3.54 StartZ=0 EndX=-3.87 EndY=6.02 EndZ=0
    g3: LineSegment StartX=-3.87 StartY=6.02 StartZ=0 EndX=6.78 EndY=6.02 EndZ=0
    g4: LineSegment StartX=6.78 StartY=6.02 StartZ=0 EndX=6.88 EndY=-3.72 EndZ=0
    g5: LineSegment StartX=6.88 StartY=-3.72 StartZ=0 EndX=3.53106 EndY=-3.54 EndZ=0
  constraints (18):
    c: Coincident(g0,g1)
    c: Vertical(g0)
    c: Horizontal(g1)
    c: PointOnObject(g1,g-3)
    c: PointOnObject(g0,g-3)
    c: Coincident(g1,g2)
    c: Coincident(g2,g3)
    c: Horizontal(g3)
    c: Coincident(g3,g4)
    c: Coincident(g4,g5)
    c: Coincident(g5,g0)
    c: DistanceY(g1,g2) = 2.48
    c: DistanceX(g2,g3) = 10.65
    c: DistanceY(g4,g3) = 9.74
    c: DistanceY(g4,g-1) = 3.72
    c: DistanceX(g-1,g3) = 6.78
    c: PointOnObject(g0,g-3)
    c: DistanceX(g-1,g4) = 6.88
FEATURE [PartDesign::Pocket] Pocket012
  BaseFeature = -> Pad004
  Direction = (0,1,-2e-16)
  Length = 43
  Length2 = 5
  Placement = pos=(0,0,0) rot=(1,0,0;1.5708rad)
  Profile = -> Sketch026
  ReferenceAxis = -> Sketch026 [N_Axis]
  Refine = true
  Suppressed = false
  Type = 0
FEATURE [Sketcher::SketchObject] Sketch027
  ArcFitTolerance = 1e-06
  AttachmentSupport = -> [Pocket012]
  ExternalGeometry = -> [Pocket012]
  FullyConstrained = true
  MakeInternals = false
  MapMode = 5
  Placement = pos=(0,-135,0) rot=(1,0,0;1.5708rad)
  sketch-geometry (6):
    g0: LineSegment StartX=-3.53106 StartY=3.54 StartZ=0 EndX=-3.53106 EndY=-3.54 EndZ=0
    g1: LineSegment StartX=-3.53106 StartY=-3.54 StartZ=0 EndX=3.53106 EndY=-3.54 EndZ=0
    g2: LineSegment StartX=-3.53106 StartY=3.54 StartZ=0 EndX=-6.79 EndY=3.54 EndZ=0
    g3: LineSegment StartX=-6.79 StartY=3.54 StartZ=0 EndX=-6.79 EndY=-6.25 EndZ=0
    g4: LineSegment StartX=-6.79 StartY=-6.25 StartZ=0 EndX=3.53106 EndY=-6.25 EndZ=0
    g5: LineSegment StartX=3.53106 StartY=-6.25 StartZ=0 EndX=3.53106 EndY=-3.54 EndZ=0
  constraints (16):
    c: Coincident(g-5,g0)
    c: PointOnObject(g0,g-3)
    c: Vertical(g0)
    c: Coincident(g0,g1)
    c: Coincident(g1,g-4)
    c: Coincident(g0,g2)
    c: Horizontal(g2)
    c: Coincident(g2,g3)
    c: Coincident(g3,g4)
    c: Horizontal(g4)
    c: Coincident(g4,g5)
    c: Coincident(g5,g1)
    c: Distance(g2,g-2) = 6.79
    c: Vertical(g3,g2)
    c: Vertical(g1,g4)
    c: DistanceY(g3,g-1) = 6.25
FEATURE [PartDesign::Pocket] Pocket013
  BaseFeature = -> Pocket012
  Direction = (0,1,-2e-16)
  Length = 43
  Length2 = 5
  Placement = pos=(0,0,0) rot=(1,0,0;1.5708rad)
  Profile = -> Sketch027
  ReferenceAxis = -> Sketch027 [N_Axis]
  Refine = true
  Suppressed = false
  Type = 0
FEATURE [PartDesign::Body] Body005  label="Shaft"
  AllowCompound = false
  Group = -> [Sketch015,Pad004,Sketch026,Pocket012,Sketch027,Pocket013]
  Origin = -> Origin006
  Placement = pos=(0,23,0) rot=(0,1,0;0rad)
  Tip = -> Pocket013
COMPONENT P13 — same part as P12; its construction recipe is shown at P12.
COMPONENT P14 — recipe-attached ("SouthMagnet001", modeled in this document).
Construction recipe (the document's own serialized feature program — sketch geometry with constraints, then the solid features built on it; lengths are millimeters unless a unit is written):

FEATURE [Sketcher::SketchObject] Sketch010
  ArcFitTolerance = 1e-06
  AttachmentSupport = -> [XZ_Plane003]
  FullyConstrained = true
  MakeInternals = false
  MapMode = 5
  Placement = pos=(0,0,0) rot=(1,0,0;1.5708rad)
  sketch-geometry (1):
    g0: Circle CenterX=0 CenterY=0 CenterZ=0 NormalX=0 NormalY=0 NormalZ=1 AngleXU=0 Radius=45
  constraints (2):
    c: Coincident(g0,g-1)
    c: Diameter(g0) = 90
FEATURE [PartDesign::Pad] Pad003
  Direction = (0,-1,2e-16)
  Length = 50
  Length2 = 10
  Placement = pos=(0,0,0) rot=(1,0,0;1.5708rad)
  Profile = -> Sketch010
  ReferenceAxis = -> Sketch010 [N_Axis]
  Refine = true
  Suppressed = false
  Type = 0
FEATURE [Sketcher::SketchObject] Sketch011
  ArcFitTolerance = 1e-06
  AttachmentSupport = -> [Pad003]
  FullyConstrained = true
  MakeInternals = false
  MapMode = 5
  Placement = pos=(0,-50,0) rot=(1,0,0;1.5708rad)
  sketch-geometry (1):
    g0: Circle CenterX=0 CenterY=0 CenterZ=0 NormalX=0 NormalY=0 NormalZ=1 AngleXU=0 Radius=35
  constraints (2):
    c: Diameter(g0) = 70
    c: Coincident(g0,g-1)
FEATURE [PartDesign::Pocket] Pocket007
  BaseFeature = -> Pad003
  Direction = (0,1,-2e-16)
  Length = 5
  Length2 = 5
  Placement = pos=(0,0,0) rot=(1,0,0;1.5708rad)
  Profile = -> Sketch011
  ReferenceAxis = -> Sketch011 [N_Axis]
  Refine = true
  Suppressed = false
  Type = 1
FEATURE [Sketcher::SketchObject] Sketch012
  ArcFitTolerance = 1e-06
  AttachmentSupport = -> [Pocket007]
  ExternalGeometry = -> [Pocket007]
  FullyConstrained = true
  MakeInternals = false
  MapMode = 5
  Placement = pos=(0,-50,0) rot=(1,0,0;1.5708rad)
  sketch-geometry (8):
    g0: LineSegment StartX=-13 StartY=45.18 StartZ=0 EndX=13 EndY=45.18 EndZ=0
    g1: LineSegment StartX=-8.2 StartY=34 StartZ=0 EndX=8.2 EndY=34 EndZ=0
    g2: LineSegment StartX=-13 StartY=45.18 StartZ=0 EndX=-8.2 EndY=34 EndZ=0
    g3: LineSegment StartX=8.2 StartY=34 StartZ=0 EndX=13 EndY=45.18 EndZ=0
    g4: LineSegment StartX=-8.2 StartY=-34 StartZ=0 EndX=8.2 EndY=-34 EndZ=0
    g5: LineSegment StartX=8.2 StartY=-34 StartZ=0 EndX=13 EndY=-45.18 EndZ=0
    g6: LineSegment StartX=13 StartY=-45.18 StartZ=0 EndX=-13 EndY=-45.18 EndZ=0
    g7: LineSegment StartX=-13 StartY=-45.18 StartZ=0 EndX=-8.2 EndY=-34 EndZ=0
  constraints (20):
    c: DistanceX(g0,g-1) = 13
    c: Symmetric(g0,g0,g-2)
    c: Symmetric(g1,g1,g-2)
    c: DistanceX(g1,g-1) = 8.2
    c: Coincident(g2,g0)
    c: Coincident(g2,g1)
    c: Coincident(g3,g1)
    c: Coincident(g3,g0)
    c: DistanceY(g-1,g1) = 34
    c: DistanceY(g-1,g0) = 45.18
    c: Coincident(g4,g5)
    c: Coincident(g5,g6)
    c: Coincident(g6,g7)
    c: Coincident(g7,g4)
    c: Vertical(g4,g1)
    c: Symmetric(g4,g4,g-2)
    c: Symmetric(g6,g5,g-2)
    c: Vertical(g6,g0)
    c: Equal(g2,g7)
    c: DistanceY(g4,g-1) = 34
FEATURE [PartDesign::Pocket] Pocket008
  BaseFeature = -> Pocket007
  Direction = (0,1,-2e-16)
  Length = 5
  Length2 = 5
  Placement = pos=(0,0,0) rot=(1,0,0;1.5708rad)
  Profile = -> Sketch012
  ReferenceAxis = -> Sketch012 [N_Axis]
  Refine = true
  Suppressed = false
  Type = 1
FEATURE [PartDesign::Body] Body003  label="SouthMagnet"
  AllowCompound = false
  Group = -> [Sketch010,Pad003,Sketch011,Pocket007,Sketch012,Pocket008]
  Origin = -> Origin003
  Placement = pos=(0,-5,0) rot=(0,1,0;3.14159rad)
  Tip = -> Pocket008
PROVENANCE & LICENSES
A FreeCAD (.FCStd) document from a public repository crawl; recipes are the document's own serialized feature recipes (and, for linked parts, companion documents' recipes).
License: as declared in the source repository (recorded in the dataset sidecar).
